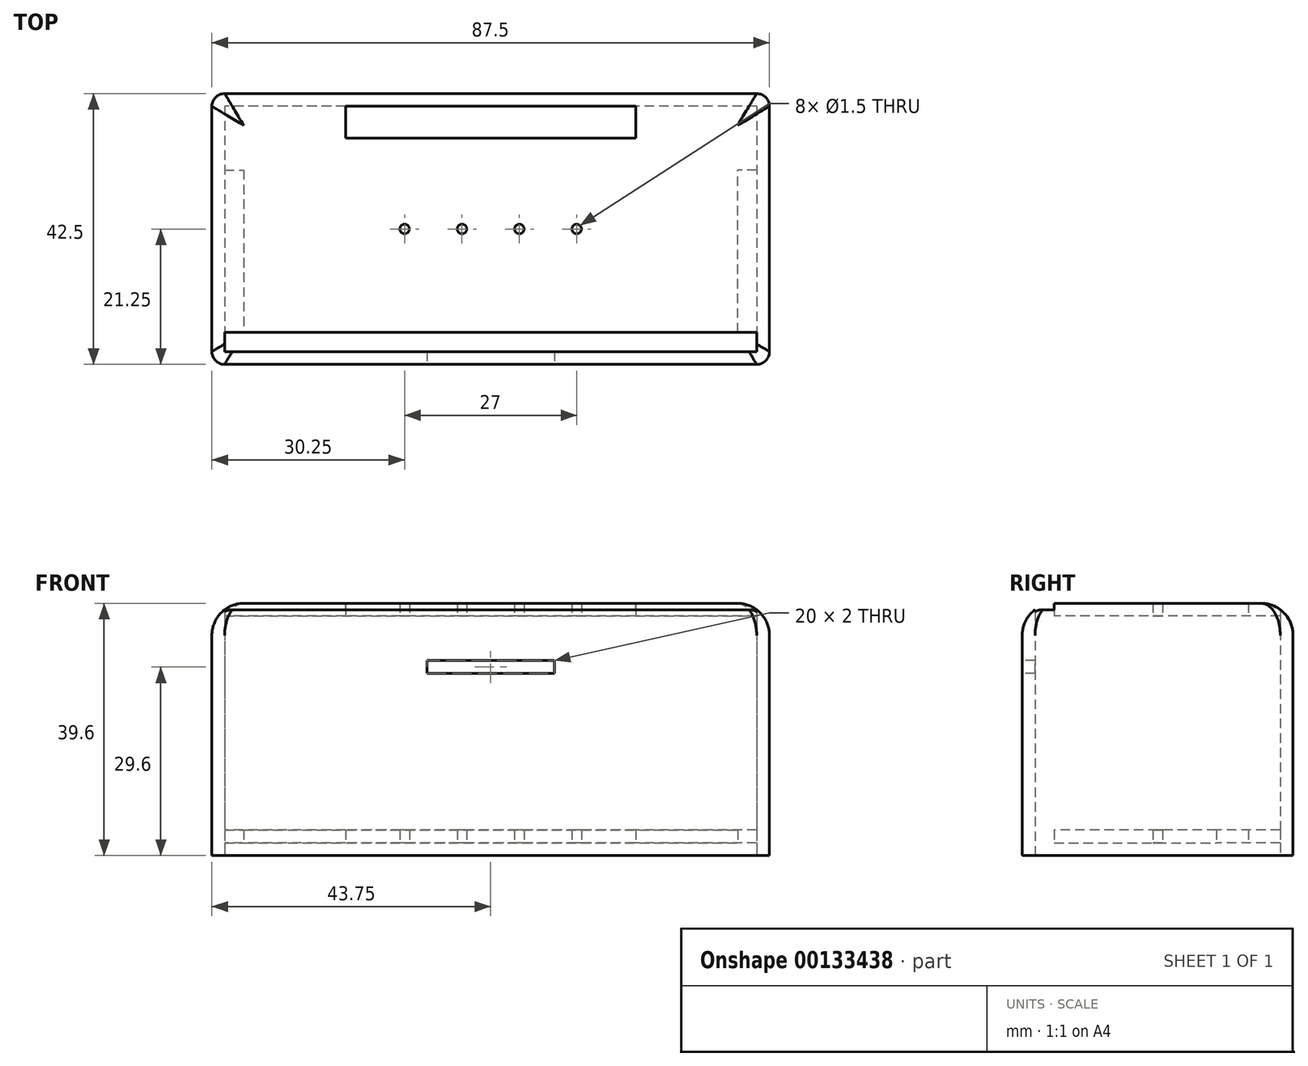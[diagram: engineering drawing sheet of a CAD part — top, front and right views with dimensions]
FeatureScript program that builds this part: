
annotation { "Feature Type Name" : "Feature", "Feature Type Description" : "" }
export const myFeature = defineFeature(function(context is Context, id is Id, definition is map)
    precondition{}
    {
        {
            var Q0;
            Q0=qCreatedBy(makeId("Top.planeOp"),FACE);
            var sketch = newSketch(context, id + "F0", { "sketchPlane" : qUnion([Q0])});
            skLineSegment(sketch, "E0.bottom", {"start": v(43.75, 21.25) * mm, "end": v(-43.75, 21.25) * mm});
            skLineSegment(sketch, "E0.top", {"start": v(43.75, -21.25) * mm, "end": v(-43.75, -21.25) * mm});
            skLineSegment(sketch, "E0.left", {"start": v(43.75, 21.25) * mm, "end": v(43.75, -21.25) * mm});
            skLineSegment(sketch, "E0.right", {"start": v(-43.75, 21.25) * mm, "end": v(-43.75, -21.25) * mm});
            skPoint(sketch, "E0.middle", {"position": v(0, 0) * mm});
            skLineSegment(sketch, "E1.0", {"start": v(-41.75, 19.25) * mm, "end": v(-41.75, -19.25) * mm});
            skLineSegment(sketch, "E1.1", {"start": v(41.75, 19.25) * mm, "end": v(-41.75, 19.25) * mm});
            skLineSegment(sketch, "E1.2", {"start": v(41.75, 19.25) * mm, "end": v(41.75, -19.25) * mm});
            skLineSegment(sketch, "E1.3", {"start": v(41.75, -19.25) * mm, "end": v(-41.75, -19.25) * mm});
            skLineSegment(sketch, "E2", {"start": v(0, 0) * mm, "end": v(4.5, 0) * mm});
            skLineSegment(sketch, "E3", {"start": v(4.5, 0) * mm, "end": v(13.5, 0) * mm});
            skCircle(sketch, "E4", {"center": v(4.5, 0) * mm, "radius": 0.75 * mm});
            skCircle(sketch, "E5", {"center": v(13.5, 0) * mm, "radius": 0.75 * mm});
            skCircle(sketch, "E6.MirrorC", {"center": v(-4.5, 0) * mm, "radius": 0.75 * mm});
            skCircle(sketch, "E7.MirrorC", {"center": v(-13.5, 0) * mm, "radius": 0.75 * mm});
            skLineSegment(sketch, "E8.bottom", {"start": v(-41.75, -19.25) * mm, "end": v(41.75, -19.25) * mm});
            skLineSegment(sketch, "E8.top", {"start": v(-41.75, -16.25) * mm, "end": v(41.75, -16.25) * mm});
            skLineSegment(sketch, "E8.left", {"start": v(-41.75, -19.25) * mm, "end": v(-41.75, -16.25) * mm});
            skLineSegment(sketch, "E8.right", {"start": v(41.75, -19.25) * mm, "end": v(41.75, -16.25) * mm});
            skLineSegment(sketch, "E9", {"start": v(-41.75, -16.25) * mm, "end": v(-38.75, -16.25) * mm});
            skLineSegment(sketch, "E10", {"start": v(-38.75, -16.25) * mm, "end": v(-38.75, 0) * mm});
            skLineSegment(sketch, "E11", {"start": v(41.75, -16.25) * mm, "end": v(38.75, -16.25) * mm});
            skLineSegment(sketch, "E12", {"start": v(38.75, -16.25) * mm, "end": v(38.75, -16.25) * mm});
            skLineSegment(sketch, "E13", {"start": v(38.75, -16.25) * mm, "end": v(38.75, 0) * mm});
            skLineSegment(sketch, "E14", {"start": v(-41.75, -16.25) * mm, "end": v(-41.75, 0) * mm});
            skLineSegment(sketch, "E15", {"start": v(-41.75, 19.25) * mm, "end": v(-22.75, 19.25) * mm});
            skLineSegment(sketch, "E16", {"start": v(-22.75, 19.25) * mm, "end": v(-22.75, 14.25) * mm});
            skLineSegment(sketch, "E17", {"start": v(41.75, 19.25) * mm, "end": v(22.75, 19.25) * mm});
            skLineSegment(sketch, "E18", {"start": v(22.75, 19.25) * mm, "end": v(22.75, 14.25) * mm});
            skLineSegment(sketch, "E19", {"start": v(22.75, 14.25) * mm, "end": v(-22.75, 14.25) * mm});
            skLineSegment(sketch, "E20", {"start": v(-41.75, 19.25) * mm, "end": v(-41.75, 9.25) * mm});
            skLineSegment(sketch, "E21", {"start": v(-41.75, 9.25) * mm, "end": v(-38.75, 9.25) * mm});
            skLineSegment(sketch, "E22", {"start": v(-38.75, 9.25) * mm, "end": v(-38.75, 0) * mm});
            skLineSegment(sketch, "E23", {"start": v(41.75, 19.25) * mm, "end": v(41.75, 9.25) * mm});
            skLineSegment(sketch, "E24", {"start": v(41.75, 9.25) * mm, "end": v(38.75, 9.25) * mm});
            skLineSegment(sketch, "E25", {"start": v(38.75, 9.25) * mm, "end": v(38.75, 0) * mm});
            skLineSegment(sketch, "E26", {"start": v(-41.75, 0) * mm, "end": v(-41.75, -19.25) * mm});
            skSolve(sketch);
        }
        {
            var Q0;
            Q0=makeQuery(id+"F0.imprint","IMPRINT",FACE,{"disambiguationData":[TD([[makeQuery(id+"F0.imprint","IMPRINT",EDGE,{"derivedFrom":sQuery(id+"F0.wireOp",EDGE,"E0.bottom")}),1.0]])]});
            extrude(context, id + "F1", {"entities" : qUnion([Q0]), "depth" : 39.6 * mm});
        }
        {
            var Q0;
            Q0=makeQuery(id+"F0.imprint","IMPRINT",FACE,{"disambiguationData":[TD([[makeQuery(id+"F0.imprint","IMPRINT",EDGE,{"derivedFrom":sQuery(id+"F0.wireOp",EDGE,"E1.0")}),1.0]])]});
            var Q1;
            Q1=makeQuery(id+"F0.imprint","IMPRINT",FACE,{"disambiguationData":[TD([[makeQuery(id+"F0.imprint","IMPRINT",EDGE,{"derivedFrom":sQuery(id+"F0.wireOp",EDGE,"E5")}),-1.0]])]});
            var Q2;
            Q2=makeQuery(id+"F0.imprint","IMPRINT",FACE,{"disambiguationData":[TD([[makeQuery(id+"F0.imprint","IMPRINT",EDGE,{"derivedFrom":sQuery(id+"F0.wireOp",EDGE,"E1.2")}),-1.0]])]});
            var Q3;
            Q3=makeQuery(id+"F0.imprint","IMPRINT",FACE,{"disambiguationData":[TD([[makeQuery(id+"F0.imprint","IMPRINT",EDGE,{"derivedFrom":sQuery(id+"F0.wireOp",EDGE,"E1.1")}),1.0]])]});
            var Q4;
            Q4=makeQuery(id+"F0.imprint","IMPRINT",FACE,{"disambiguationData":[TD([[makeQuery(id+"F0.imprint","IMPRINT",EDGE,{"derivedFrom":sQuery(id+"F0.wireOp",EDGE,"E8.bottom")}),1.0]])]});
            extrude(context, id + "F2", {"entities" : qUnion([Q0, Q1, Q2, Q3, Q4]), "operationType" : NewBodyOperationType.ADD, "depth" : 39.6 * mm, "hasSecondDirection" : true, "secondDirectionOppositeDirection" : false, "secondDirectionDepth" : 37.6 * mm});
        }
        {
            var Q0;
            Q0=qSketchRegion(id+"F0",true);
            var Q1;
            Q1=makeQuery(id+"F0.imprint","IMPRINT",FACE,{"disambiguationData":[TD([[makeQuery(id+"F0.imprint","IMPRINT",EDGE,{"derivedFrom":sQuery(id+"F0.wireOp",EDGE,"E9")}),1.0]])]});
            var Q2;
            Q2=makeQuery(id+"F0.imprint","IMPRINT",FACE,{"disambiguationData":[TD([[makeQuery(id+"F0.imprint","IMPRINT",EDGE,{"derivedFrom":sQuery(id+"F0.wireOp",EDGE,"E8.bottom")}),1.0]])]});
            var Q3;
            {var subQ0=sQuery(id+"F0.wireOp",EDGE,"E11");Q3=makeQuery(id+"F0.imprint","IMPRINT",FACE,{"disambiguationData":[TD([[makeQuery(id+"F0.imprint","IMPRINT",EDGE,{"derivedFrom":subQ0}),-1.0]])]});}
            var Q4;
            Q4=makeQuery(id+"F0.imprint","IMPRINT",FACE,{"disambiguationData":[TD([[makeQuery(id+"F0.imprint","IMPRINT",EDGE,{"derivedFrom":sQuery(id+"F0.wireOp",EDGE,"E1.1")}),1.0]])]});
            extrude(context, id + "F3", {"entities" : qUnion([Q0, Q1, Q2, Q3, Q4]), "operationType" : NewBodyOperationType.ADD, "depth" : 4 * mm, "hasSecondDirection" : true, "secondDirectionOppositeDirection" : false, "secondDirectionDepth" : 2 * mm});
        }
        {
            var Q0;
            Q0=makeQuery(id+"F1.opExtrude","SWEPT_EDGE",EDGE,{"disambiguationData":[OSD([sQuery(id+"F0.wireOp",EDGE,"E0.bottom"),sQuery(id+"F0.wireOp",EDGE,"E0.left")])]});
            var Q1;
            Q1=makeQuery(id+"F1.opExtrude","SWEPT_EDGE",EDGE,{"disambiguationData":[OSD([sQuery(id+"F0.wireOp",EDGE,"E0.bottom"),sQuery(id+"F0.wireOp",EDGE,"E0.right")])]});
            var Q2;
            Q2=makeQuery(id+"F1.opExtrude","SWEPT_EDGE",EDGE,{"disambiguationData":[OSD([sQuery(id+"F0.wireOp",EDGE,"E0.top"),sQuery(id+"F0.wireOp",EDGE,"E0.left")])]});
            var Q3;
            Q3=makeQuery(id+"F1.opExtrude","SWEPT_EDGE",EDGE,{"disambiguationData":[OSD([sQuery(id+"F0.wireOp",EDGE,"E0.top"),sQuery(id+"F0.wireOp",EDGE,"E0.right")])]});
            fillet(context, id + "F4", {"entities" : qUnion([Q0, Q1, Q2, Q3]), "radius" : 2 * mm, "tangentPropagation" : true, "allowEdgeOverflow" : false});
        }
        {
            var Q0;
            Q0=makeQuery(id+"F1.opExtrude","CAP_EDGE",EDGE,{"disambiguationData":[OSD([sQuery(id+"F0.wireOp",EDGE,"E0.left")])],"isStart":false});
            fillet(context, id + "F5", {"entities" : qUnion([Q0]), "radius" : 5 * mm, "tangentPropagation" : true, "allowEdgeOverflow" : false});
        }
        {
            var Q0;
            Q0=makeQuery(id+"F1.opExtrude","SWEPT_FACE",FACE,{"disambiguationData":[OSD([sQuery(id+"F0.wireOp",EDGE,"E0.top")])]});
            var sketch = newSketch(context, id + "F6", { "sketchPlane" : qUnion([Q0])});
            skLineSegment(sketch, "E27", {"start": v(0, 0) * mm, "end": v(0, 34.6) * mm});
            skLineSegment(sketch, "E28", {"start": v(0, 34.6) * mm, "end": v(0, 29.6) * mm});
            skLineSegment(sketch, "E29.bottom", {"start": v(10, 28.6) * mm, "end": v(-10, 28.6) * mm});
            skLineSegment(sketch, "E29.top", {"start": v(10, 30.6) * mm, "end": v(-10, 30.6) * mm});
            skLineSegment(sketch, "E29.left", {"start": v(10, 28.6) * mm, "end": v(10, 30.6) * mm});
            skLineSegment(sketch, "E29.right", {"start": v(-10, 28.6) * mm, "end": v(-10, 30.6) * mm});
            skPoint(sketch, "E29.middle", {"position": v(0, 29.6) * mm});
            skSolve(sketch);
        }
        {
            var Q0;
            {var subQ0=sQuery(id+"F6.wireOp",EDGE,"E29.right");Q0=makeQuery(id+"F6.imprint","IMPRINT",FACE,{"disambiguationData":[TD([[makeQuery(id+"F6.imprint","IMPRINT",EDGE,{"derivedFrom":subQ0}),-1.0]])]});}
            var Q1;
            {var subQ0=sQuery(id+"F6.wireOp",EDGE,"E29.left");Q1=makeQuery(id+"F6.imprint","IMPRINT",FACE,{"disambiguationData":[TD([[makeQuery(id+"F6.imprint","IMPRINT",EDGE,{"derivedFrom":subQ0}),1.0]])]});}
            extrude(context, id + "F7", {"entities" : qUnion([Q0, Q1]), "operationType" : NewBodyOperationType.REMOVE, "oppositeDirection" : true, "depth" : 2 * mm});
        }
    });
